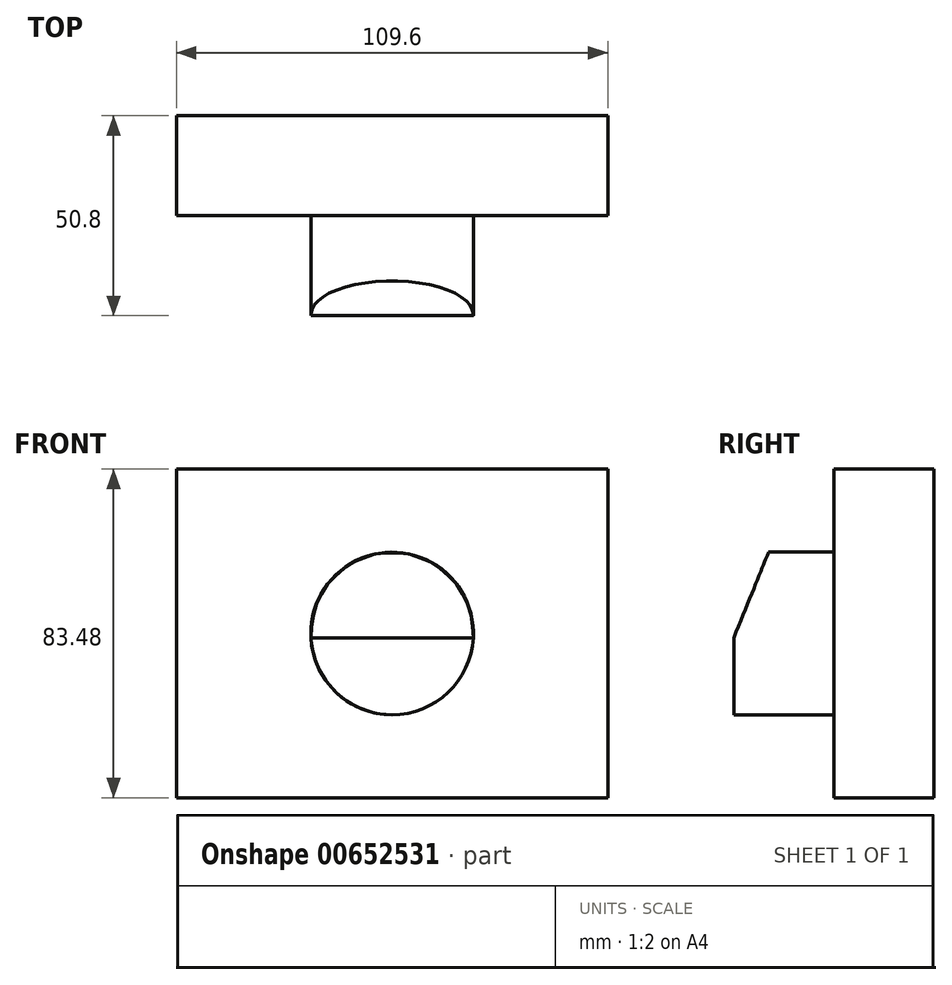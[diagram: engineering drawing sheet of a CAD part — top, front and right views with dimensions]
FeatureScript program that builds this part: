
annotation { "Feature Type Name" : "Feature", "Feature Type Description" : "" }
export const myFeature = defineFeature(function(context is Context, id is Id, definition is map)
    precondition{}
    {
        {
            var Q0;
            Q0=qCreatedBy(makeId("Front.planeOp"),FACE);
            var sketch = newSketch(context, id + "F0", { "sketchPlane" : qUnion([Q0])});
            skLineSegment(sketch, "E0.bottom", {"start": v(54.8, 41.74) * mm, "end": v(-54.8, 41.74) * mm});
            skLineSegment(sketch, "E0.top", {"start": v(54.8, -41.74) * mm, "end": v(-54.8, -41.74) * mm});
            skLineSegment(sketch, "E0.left", {"start": v(54.8, 41.74) * mm, "end": v(54.8, -41.74) * mm});
            skLineSegment(sketch, "E0.right", {"start": v(-54.8, 41.74) * mm, "end": v(-54.8, -41.74) * mm});
            skPoint(sketch, "E0.middle", {"position": v(0, 0) * mm});
            skSolve(sketch);
        }
        {
            var Q0;
            Q0 = qSketchRegion(id + "F0", true);
            extrude(context, id + "F1", {"entities" : qUnion([Q0]), "depth" : 25.4 * mm, "offsetDistance" : 25.4 * mm});
        }
        {
            var Q0;
            Q0=makeQuery(id+"F1.opExtrude","CAP_FACE",FACE,{"disambiguationData":[OSD([sQuery(id+"F0.wireOp",EDGE,"E0.bottom"),sQuery(id+"F0.wireOp",EDGE,"E0.top"),sQuery(id+"F0.wireOp",EDGE,"E0.left"),sQuery(id+"F0.wireOp",EDGE,"E0.right")])],"isStart":false});
            var sketch = newSketch(context, id + "F2", { "sketchPlane" : qUnion([Q0])});
            skCircle(sketch, "E1", {"center": v(0, 0) * mm, "radius": 20.65 * mm});
            skSolve(sketch);
        }
        {
            var Q0;
            Q0 = qSketchRegion(id + "F2", true);
            extrude(context, id + "F3", {"entities" : qUnion([Q0]), "operationType" : NewBodyOperationType.ADD, "depth" : 25.4 * mm, "offsetDistance" : 25.4 * mm});
        }
        {
            var Q0;
            Q0=qCreatedBy(makeId("Right.planeOp"),FACE);
            var sketch = newSketch(context, id + "F4", { "sketchPlane" : qUnion([Q0])});
            skLineSegment(sketch, "E2", {"start": v(-65.9, -38.19) * mm, "end": v(-65.9, 37.03) * mm});
            skLineSegment(sketch, "E3", {"start": v(-65.9, 37.03) * mm, "end": v(-35.28, 37.03) * mm});
            skLineSegment(sketch, "E4", {"start": v(-35.28, 37.03) * mm, "end": v(-65.9, -38.19) * mm});
            skSolve(sketch);
        }
        {
            var Q0;
            Q0 = qSketchRegion(id + "F4", true);
            extrude(context, id + "F5", {"entities" : qUnion([Q0]), "operationType" : NewBodyOperationType.REMOVE, "endBound" : BoundingType.SYMMETRIC, "oppositeDirection" : true, "depth" : 50.8 * mm, "offsetDistance" : 25.4 * mm});
        }
    });
